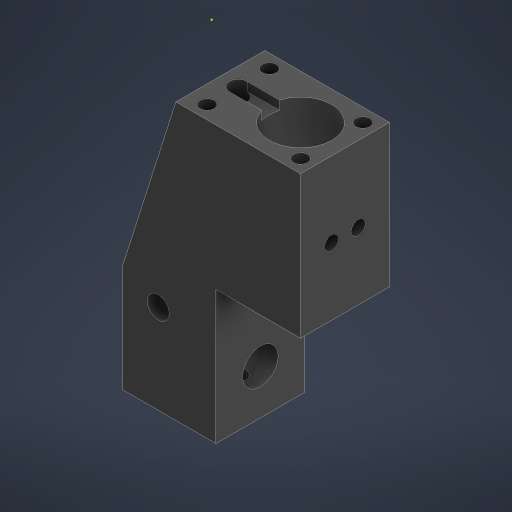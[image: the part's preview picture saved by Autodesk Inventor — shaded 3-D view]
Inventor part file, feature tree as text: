
AUTODESK INVENTOR PART (.ipt)
format: ipt  version: 2023 (Build 270158000, 158)  size: 363,008 bytes
history: native  units: mm
features: sketch x11, hole x9, extrude x3, projected_geometry x2, plane x1
ambient origin geometry x8: Origin, YZ Plane, XZ Plane, XY Plane, X Axis, Y Axis, Z Axis, Center Point
bodies: Solid1 (feature_tree)
feature tree (26):
  extrude  "Extrusion1"  Depth=21.0mm
  hole  "Hole1"  [1 undecoded]
  sketch  "Sketch3"  dims[d4=32.0mm d5=28.0mm]
  hole  "Hole2"  [1 undecoded]
  sketch  "Sketch4"  dims[d6=20.0mm d7=0.0mm d8=10.0mm]
  extrude  "Extrusion2"  Depth=10.0mm
  extrude  "Extrusion3"  Depth=3.0mm
  hole  "Hole3"  [1 undecoded]
  hole  "Hole4"  [1 undecoded]
  plane  "Work Plane1"
  hole  "Hole5"  [1 undecoded]
  hole  "Hole6"  [1 undecoded]
  hole  "Hole7"  [1 undecoded]
  hole  "Hole8"  [1 undecoded]
  hole  "Hole9"  [1 undecoded]
  sketch  "Sketch1"  dims[d0=24.0mm d1=21.0mm]
  sketch  "Sketch2"  dims[d2=30.0mm d3=19.0mm]
  sketch  "Sketch5"  dims[d9=14.0mm d10=6.0mm d11=4.0mm d12=2.0mm d13=90.0deg d14=3.0mm d15=0.0mm d18=3.0mm]
  sketch  "Sketch6"  dims[d19=3.0mm d20=3.0mm]
  sketch  "Sketch7"  dims[d21=3.0mm d22=21.0mm]
  sketch  "Sketch8"  dims[d23=7.0mm]
  sketch  "Sketch9"  dims[d24=3.2mm d25=6.0mm d26=4.0mm d27=2.0mm d28=90.0deg d29=6.0mm d30=0.0mm d32=4.0mm]
  sketch  "Sketch10"  dims[d33=2.0mm d34=0.0mm d35=30.0mm d36=0.0mm]
  sketch  "Sketch11"  dims[d37=10.0mm d38=8.0mm d39=6.0mm d40=10.0mm d41=2.0mm d42=90.0deg d43=3.0mm d44=0.0mm d45=20.0mm d46=8.0mm d47=5.0mm d48=6.0mm d49=10.0mm d50=2.0mm d51=90.0deg d52=3.0mm d53=0.0mm d54=-30.0mm d55=2.5mm d56=2.5mm d57=6.0mm d58=10.0mm d59=2.0mm d60=90.0deg d61=18.0mm d62=20.594885mm d63=3.0mm d64=6.0mm d65=10.0mm d66=2.0mm d67=90.0deg d68=9.0mm d69=20.594885mm d70=3.0mm d71=6.0mm d72=10.0mm d73=2.0mm d74=90.0deg d75=9.0mm d76=20.594885mm d77=8.0mm d78=8.0mm d79=4.0mm d80=6.0mm d81=10.0mm d82=2.0mm d83=90.0deg d84=6.0mm d85=20.594885mm d86=17.0mm d87=3.0mm d88=6.0mm d89=3.2mm d90=6.0mm d91=10.0mm d92=2.0mm d93=90.0deg d94=3.0mm d95=20.594885mm]
  projected_geometry  "Project Cut Edges1"
  projected_geometry  "Project Cut Edges2"
note: 9 required parameter values undecoded (feature->parameter linkage not recoverable at this tier; creation-order binding heuristic only, values carry confidence <= 0.55)
